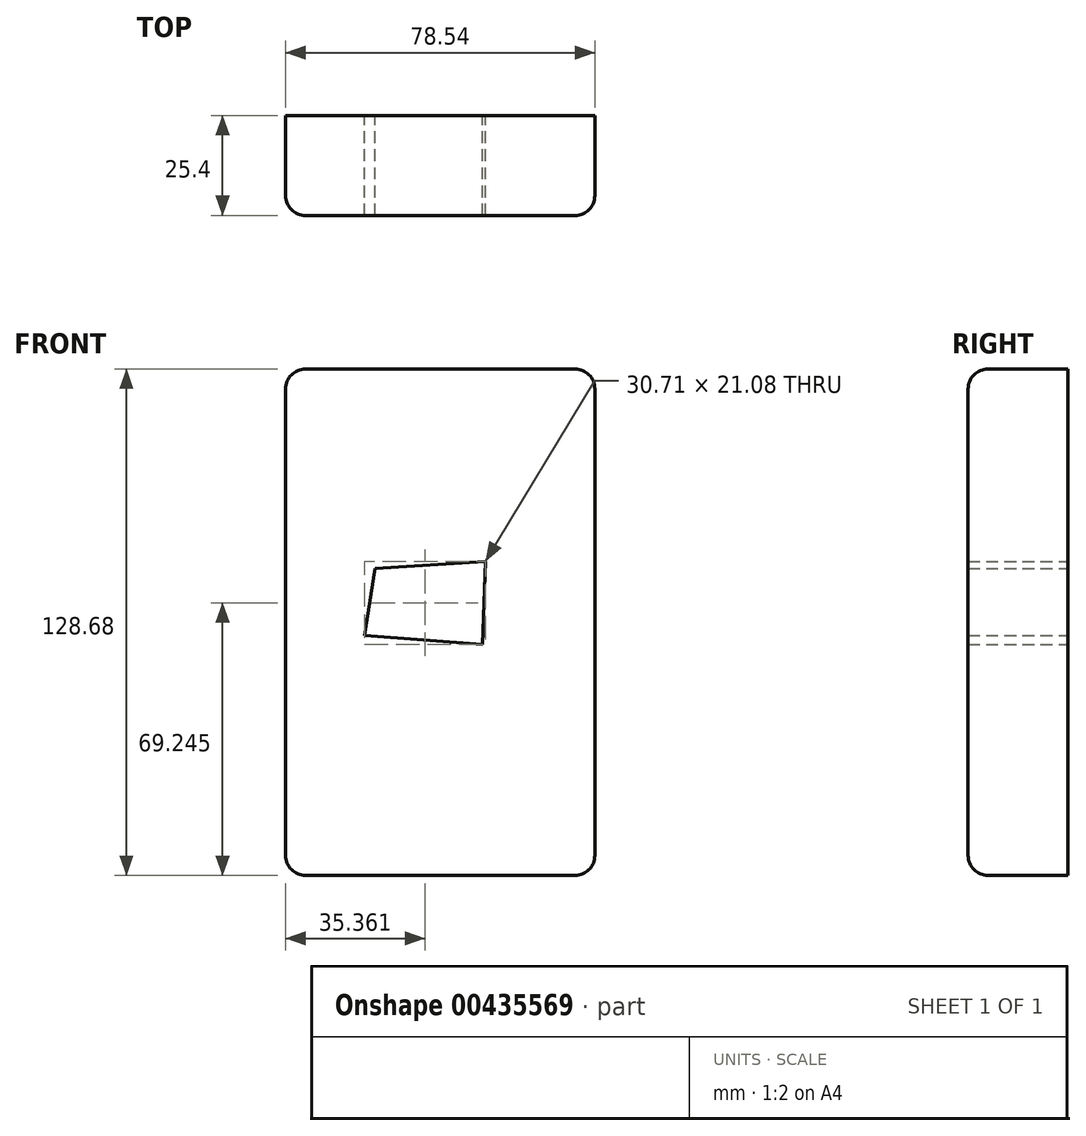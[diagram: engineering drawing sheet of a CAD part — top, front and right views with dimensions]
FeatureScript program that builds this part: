
annotation { "Feature Type Name" : "Feature", "Feature Type Description" : "" }
export const myFeature = defineFeature(function(context is Context, id is Id, definition is map)
    precondition{}
    {
        {
            var Q0;
            Q0=qCreatedBy(makeId("Front.planeOp"),FACE);
            var sketch = newSketch(context, id + "F0", { "sketchPlane" : qUnion([Q0])});
            skLineSegment(sketch, "E0.bottom", {"start": v(-44.25, 67.66) * mm, "end": v(34.3, 67.66) * mm});
            skLineSegment(sketch, "E0.top", {"start": v(-44.25, -61.02) * mm, "end": v(34.3, -61.02) * mm});
            skLineSegment(sketch, "E0.left", {"start": v(-44.25, 67.66) * mm, "end": v(-44.25, -61.02) * mm});
            skLineSegment(sketch, "E0.right", {"start": v(34.3, 67.66) * mm, "end": v(34.3, -61.02) * mm});
            skSolve(sketch);
        }
        {
            var Q0;
            Q0=makeQuery(id+"F0.imprint","IMPRINT",FACE,{"disambiguationData":[TD([[makeQuery(id+"F0.imprint","IMPRINT",EDGE,{"derivedFrom":sQuery(id+"F0.wireOp",EDGE,"E0.bottom")}),-1.0]])]});
            extrude(context, id + "F1", {"entities" : qUnion([Q0]), "depth" : 25.4 * mm});
        }
        {
            var Q0;
            Q0=makeQuery(id+"F1.opExtrude","CAP_EDGE",EDGE,{"disambiguationData":[OSD([sQuery(id+"F0.wireOp",EDGE,"E0.bottom")])],"isStart":false});
            fillet(context, id + "F2", {"entities" : qUnion([Q0]), "radius" : 5.08 * mm, "tangentPropagation" : true, "allowEdgeOverflow" : false});
        }
        {
            var Q0;
            Q0=makeQuery(id+"F1.opExtrude","CAP_EDGE",EDGE,{"disambiguationData":[OSD([sQuery(id+"F0.wireOp",EDGE,"E0.left")])],"isStart":false});
            fillet(context, id + "F3", {"entities" : qUnion([Q0]), "radius" : 5.08 * mm, "tangentPropagation" : true, "allowEdgeOverflow" : false});
        }
        {
            var Q0;
            Q0=makeQuery(id+"F1.opExtrude","CAP_EDGE",EDGE,{"disambiguationData":[OSD([sQuery(id+"F0.wireOp",EDGE,"E0.right")])],"isStart":false});
            fillet(context, id + "F4", {"entities" : qUnion([Q0]), "radius" : 5.08 * mm, "tangentPropagation" : true, "allowEdgeOverflow" : false});
        }
        {
            var Q0;
            Q0=makeQuery(id+"F1.opExtrude","CAP_EDGE",EDGE,{"disambiguationData":[OSD([sQuery(id+"F0.wireOp",EDGE,"E0.top")])],"isStart":false});
            fillet(context, id + "F5", {"entities" : qUnion([Q0]), "radius" : 5.08 * mm, "tangentPropagation" : true, "allowEdgeOverflow" : false});
        }
        {
            var Q0;
            Q0=makeQuery(id+"F1.opExtrude","CAP_FACE",FACE,{"disambiguationData":[OSD([sQuery(id+"F0.wireOp",EDGE,"E0.bottom"),sQuery(id+"F0.wireOp",EDGE,"E0.top"),sQuery(id+"F0.wireOp",EDGE,"E0.left"),sQuery(id+"F0.wireOp",EDGE,"E0.right")])],"isStart":false});
            shell(context, id + "F6", {"entities" : qUnion([Q0]), "thickness" : 2819.4 * mm});
        }
        {
            var Q0;
            Q0=qCreatedBy(makeId("Front.planeOp"),FACE);
            var sketch = newSketch(context, id + "F7", { "sketchPlane" : qUnion([Q0])});
            skLineSegment(sketch, "E1", {"start": v(6.46, 18.77) * mm, "end": v(-21.53, 16.97) * mm});
            skLineSegment(sketch, "E2", {"start": v(-21.53, 16.97) * mm, "end": v(-24.24, 0) * mm});
            skLineSegment(sketch, "E3", {"start": v(-24.24, 0) * mm, "end": v(5.75, -2.32) * mm});
            skLineSegment(sketch, "E4", {"start": v(5.75, -2.32) * mm, "end": v(6.46, 18.77) * mm});
            skSolve(sketch);
        }
        {
            var Q0;
            Q0=makeQuery(id+"F7.imprint","IMPRINT",FACE,{"disambiguationData":[TD([[makeQuery(id+"F7.imprint","IMPRINT",EDGE,{"derivedFrom":sQuery(id+"F7.wireOp",EDGE,"E1")}),1.0]])]});
            extrude(context, id + "F8", {"entities" : qUnion([Q0]), "operationType" : NewBodyOperationType.REMOVE, "depth" : 25.4 * mm});
        }
    });
